# Revit family: 293P
name_source: partatom
category: Pipe Accessories
units: mm (PartAtom-declared; Revit-internal decimal feet)

## family parameters
Always vertical = Yes
Cut with Voids When Loaded = No
OmniClass Number = 23.45.00.00
OmniClass Title = Sanitary, Laundry, and Cleaning Equipment
Part Type = Valve - Breaks Into
Round Connector Dimension = Use Diameter
Shared = No
Work Plane-Based = No

## types (1)
- 293P
    Ball = Chrome-plated brass CW617N
    Description = IDEAL DVGW BALL VALVE, FULL FLOW
    Handle = Green
    Handle Screw = Screw
    ITAP_body_material = Nikel-plated brass CW617N_G
    Male end adapter = Nickel-plated brass CW617N
    Manufacturer = ITAP S.p.A.
    Model = 293P
    O ring = Viton
    O-ring = NBR
    Screw = Zinc-plated steel C4C
    Seat = P.T.F.E.
    Stem = Brass CW614N
    T handle = Varnished  aluminium
    Table = ITAP
    URL = https://www.itap.it

## geometry (parser evidence)
native form markers: Sweep x10
no freeform markers — native parametric forms only
